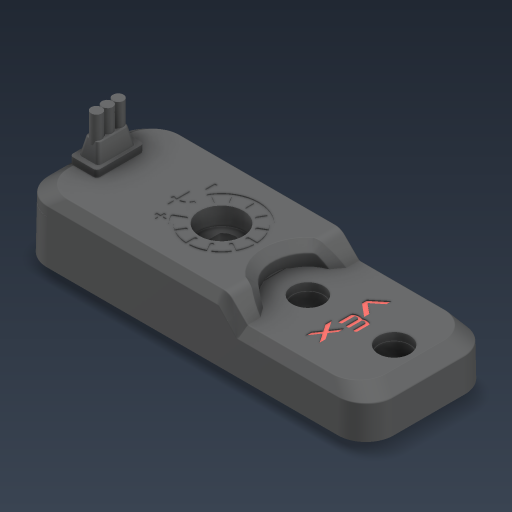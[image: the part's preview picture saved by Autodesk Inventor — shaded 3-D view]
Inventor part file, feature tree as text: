
AUTODESK INVENTOR PART (.ipt)
format: ipt  version: 2023 (Build 270158000, 158)  size: 2,946,048 bytes
history: native  units: in
note: dims shown in document units (in); Inventor stores cm internally (conversion verified against a paired STEP export)
features: other x4, extrude x1, sketch x1
ambient origin geometry x8: Origin, YZ Plane, XZ Plane, XY Plane, X Axis, Y Axis, Z Axis, Center Point
bodies: Solid1 (feature_tree), Solid2 (feature_tree), Solid3 (feature_tree), Solid4 (feature_tree)
feature tree (6):
  extrude  "Extrusion1"  [1 undecoded]
  sketch  "Sketch1"  dims[d0=3.3465in d1=0.0in]
  other  "276-7417-900 Web_1:1"
  other  "276-7417-003 Web_2:1"
  other  "276-7417-002 Web_3:1"
  other  "276-7417-001 Web_4:1"
note: 1 required parameter value undecoded (feature->parameter linkage not recoverable at this tier; creation-order binding heuristic only, values carry confidence <= 0.55)
